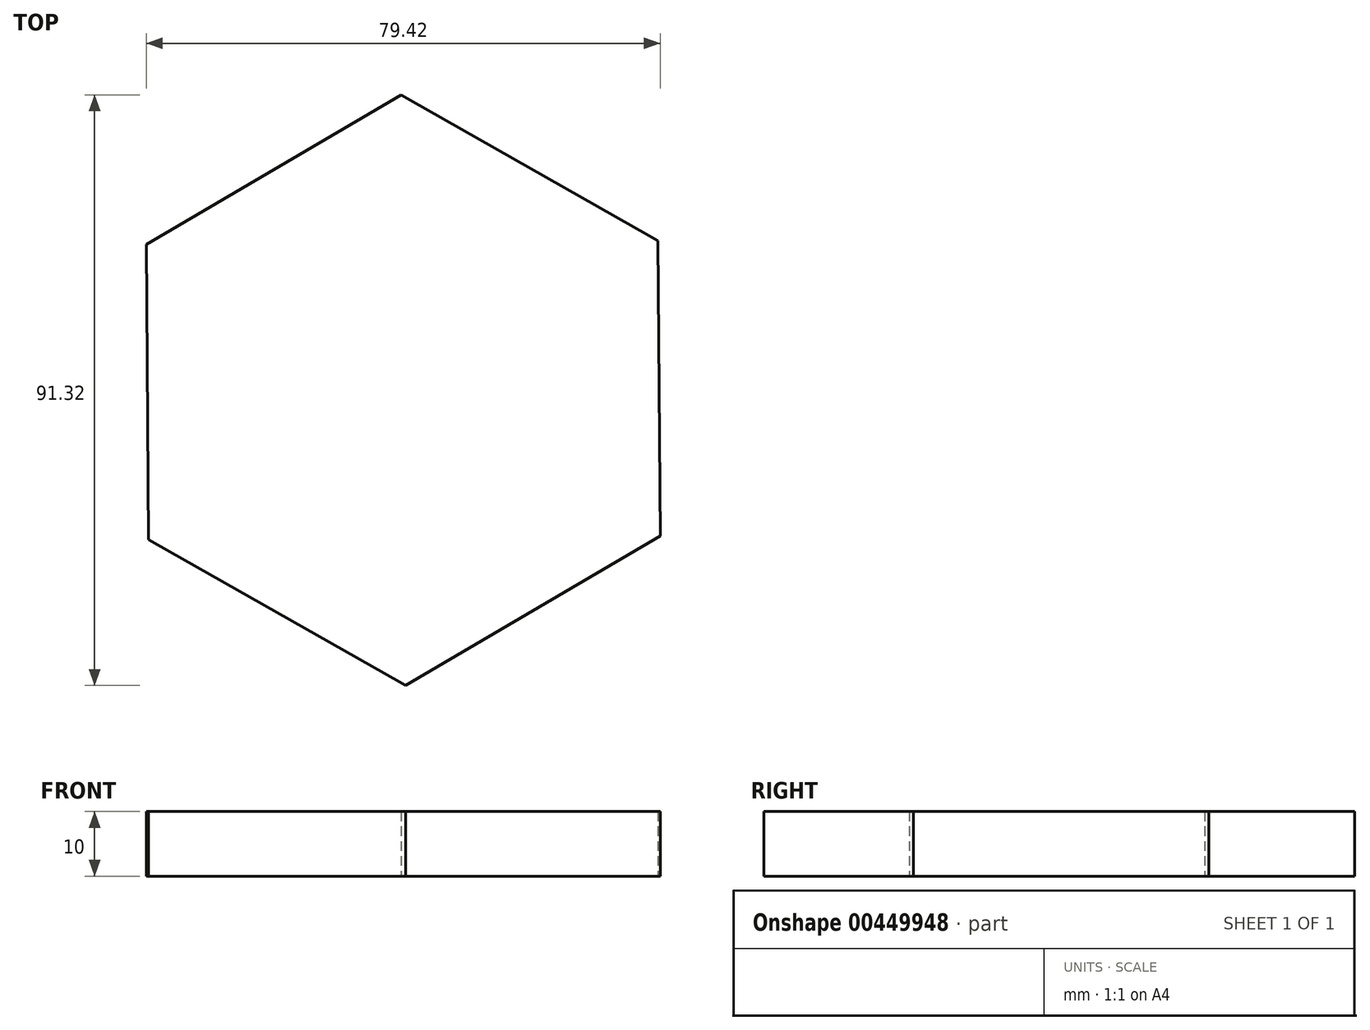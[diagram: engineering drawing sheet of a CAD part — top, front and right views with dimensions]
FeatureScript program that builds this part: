
annotation { "Feature Type Name" : "Feature", "Feature Type Description" : "" }
export const myFeature = defineFeature(function(context is Context, id is Id, definition is map)
    precondition{}
    {
        {
            var Q0;
            Q0=qCreatedBy(makeId("Top.planeOp"),FACE);
            var sketch = newSketch(context, id + "F0", { "sketchPlane" : qUnion([Q0])});
            skCircle(sketch, "E0.cCircle", {"center": v(0, 0) * mm, "radius": 39.54 * mm, "construction": true});
            skLineSegment(sketch, "E0.0", {"start": v(39.7, -22.53) * mm, "end": v(0.34, -45.66) * mm});
            skLineSegment(sketch, "E0.1", {"start": v(0.34, -45.66) * mm, "end": v(-39.37, -23.12) * mm});
            skLineSegment(sketch, "E0.2", {"start": v(-39.37, -23.12) * mm, "end": v(-39.7, 22.53) * mm});
            skLineSegment(sketch, "E0.3", {"start": v(-39.7, 22.53) * mm, "end": v(-0.34, 45.66) * mm});
            skLineSegment(sketch, "E0.4", {"start": v(-0.34, 45.66) * mm, "end": v(39.37, 23.12) * mm});
            skLineSegment(sketch, "E0.5", {"start": v(39.37, 23.12) * mm, "end": v(39.7, -22.53) * mm});
            skPoint(sketch, "E0.0.midPoint", {"position": v(20.03, -34.1) * mm});
            skSolve(sketch);
        }
        {
            var Q0;
            Q0=makeQuery(id+"F0.imprint","IMPRINT",FACE,{"disambiguationData":[TD([[makeQuery(id+"F0.imprint","IMPRINT",EDGE,{"derivedFrom":sQuery(id+"F0.wireOp",EDGE,"E0.0")}),-1.0]])]});
            extrude(context, id + "F1", {"entities" : qUnion([Q0]), "depth" : 10 * mm});
        }
    });
